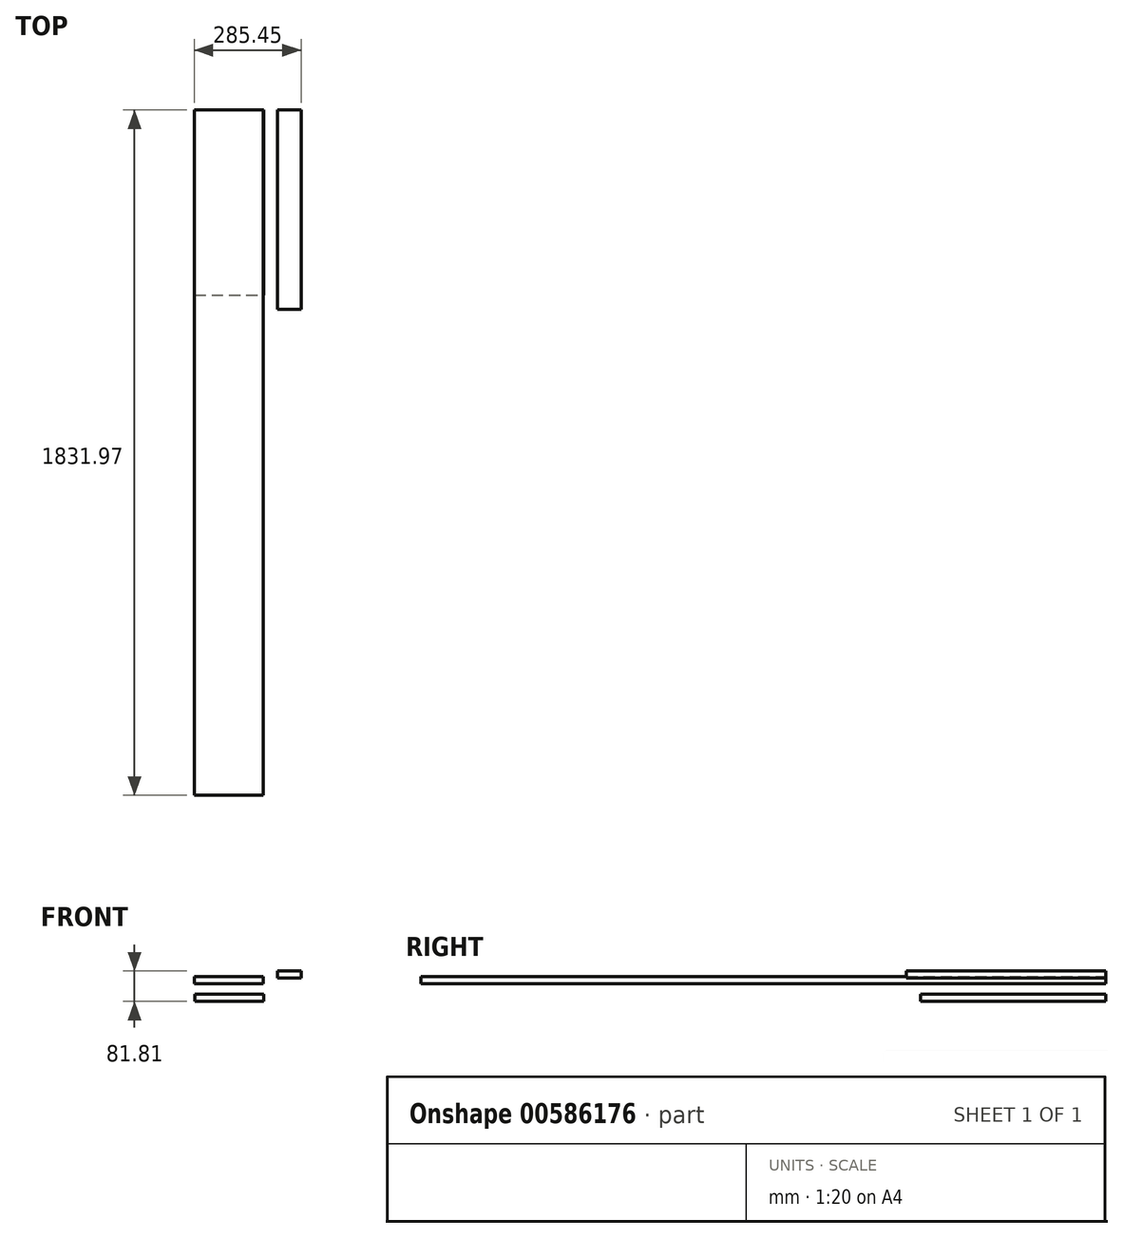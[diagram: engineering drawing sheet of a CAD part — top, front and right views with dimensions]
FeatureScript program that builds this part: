
annotation { "Feature Type Name" : "Feature", "Feature Type Description" : "" }
export const myFeature = defineFeature(function(context is Context, id is Id, definition is map)
    precondition{}
    {
        {
            var Q0;
            Q0=qCreatedBy(makeId("Front.planeOp"),FACE);
            var sketch = newSketch(context, id + "F0", { "sketchPlane" : qUnion([Q0])});
            skLineSegment(sketch, "E0.bottom", {"start": v(-214.93, 46.86) * mm, "end": v(-30.78, 46.86) * mm});
            skLineSegment(sketch, "E0.top", {"start": v(-214.93, 27.8) * mm, "end": v(-30.78, 27.8) * mm});
            skLineSegment(sketch, "E0.left", {"start": v(-214.93, 46.86) * mm, "end": v(-214.93, 27.8) * mm});
            skLineSegment(sketch, "E0.right", {"start": v(-30.78, 46.86) * mm, "end": v(-30.78, 27.8) * mm});
            skLineSegment(sketch, "E1.bottom", {"start": v(-31.38, 94.33) * mm, "end": v(-215.53, 94.33) * mm});
            skLineSegment(sketch, "E1.top", {"start": v(-31.38, 75.28) * mm, "end": v(-215.53, 75.28) * mm});
            skLineSegment(sketch, "E1.left", {"start": v(-31.38, 94.33) * mm, "end": v(-31.38, 75.28) * mm});
            skLineSegment(sketch, "E1.right", {"start": v(-215.53, 94.33) * mm, "end": v(-215.53, 75.28) * mm});
            skLineSegment(sketch, "E2.bottom", {"start": v(6.42, 90.57) * mm, "end": v(69.92, 90.57) * mm});
            skLineSegment(sketch, "E2.top", {"start": v(6.42, 109.62) * mm, "end": v(69.92, 109.62) * mm});
            skLineSegment(sketch, "E2.left", {"start": v(6.42, 90.57) * mm, "end": v(6.42, 109.62) * mm});
            skLineSegment(sketch, "E2.right", {"start": v(69.92, 90.57) * mm, "end": v(69.92, 109.62) * mm});
            skSolve(sketch);
        }
        {
            var Q0;
            Q0=makeQuery(id+"F0.imprint","IMPRINT",FACE,{"disambiguationData":[TD([[makeQuery(id+"F0.imprint","IMPRINT",EDGE,{"derivedFrom":sQuery(id+"F0.wireOp",EDGE,"E1.bottom")}),1.0]])]});
            extrude(context, id + "F1", {"entities" : qUnion([Q0]), "depth" : 1831.97 * mm, "offsetDistance" : 25.4 * mm});
        }
        {
            var Q0;
            Q0=makeQuery(id+"F0.imprint","IMPRINT",FACE,{"disambiguationData":[TD([[makeQuery(id+"F0.imprint","IMPRINT",EDGE,{"derivedFrom":sQuery(id+"F0.wireOp",EDGE,"E2.bottom")}),1.0]])]});
            extrude(context, id + "F2", {"entities" : qUnion([Q0]), "depth" : 533.4 * mm, "offsetDistance" : 25.4 * mm});
        }
        {
            var Q0;
            Q0=makeQuery(id+"F0.imprint","IMPRINT",FACE,{"disambiguationData":[TD([[makeQuery(id+"F0.imprint","IMPRINT",EDGE,{"derivedFrom":sQuery(id+"F0.wireOp",EDGE,"E0.bottom")}),-1.0]])]});
            extrude(context, id + "F3", {"entities" : qUnion([Q0]), "depth" : 495.3 * mm, "offsetDistance" : 25.4 * mm});
        }
        {
            var Q0;
            Q0=makeQuery(id+"F1.opExtrude","SWEPT_FACE",FACE,{"disambiguationData":[OSD([sQuery(id+"F0.wireOp",EDGE,"E1.right")])]});
            var sketch = newSketch(context, id + "F4", { "sketchPlane" : qUnion([Q0])});
            skLineSegment(sketch, "E3", {"start": v(1781.18, 94.33) * mm, "end": v(1781.18, 75.28) * mm, "construction": true});
            skLineSegment(sketch, "E4", {"start": v(1527.18, 94.33) * mm, "end": v(1527.18, 75.28) * mm, "construction": true});
            skLineSegment(sketch, "E5", {"start": v(1222.38, 94.33) * mm, "end": v(1222.38, 75.28) * mm, "construction": true});
            skLineSegment(sketch, "E6", {"start": v(815.98, 94.33) * mm, "end": v(815.98, 75.28) * mm, "construction": true});
            skLineSegment(sketch, "E7", {"start": v(409.58, 94.33) * mm, "end": v(409.58, 75.28) * mm, "construction": true});
            skLineSegment(sketch, "E8", {"start": v(53.98, 94.33) * mm, "end": v(53.98, 75.28) * mm, "construction": true});
            skSolve(sketch);
        }
    });
